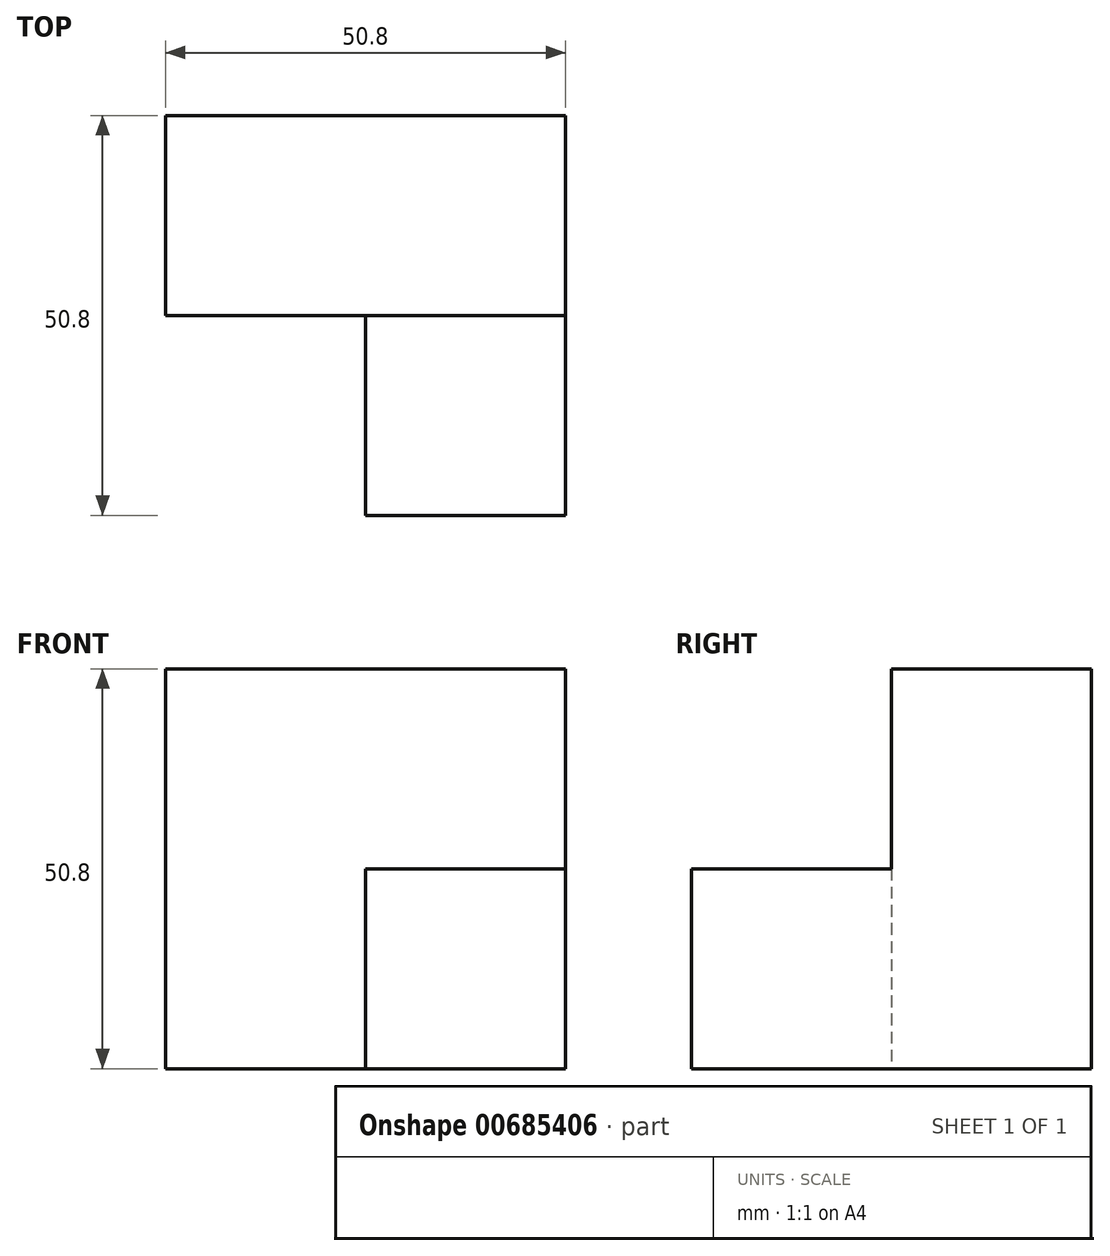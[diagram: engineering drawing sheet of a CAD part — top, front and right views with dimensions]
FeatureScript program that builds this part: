
annotation { "Feature Type Name" : "Feature", "Feature Type Description" : "" }
export const myFeature = defineFeature(function(context is Context, id is Id, definition is map)
    precondition{}
    {
        {
            var Q0;
            Q0=qCreatedBy(makeId("Front.planeOp"),FACE);
            var sketch = newSketch(context, id + "F0", { "sketchPlane" : qUnion([Q0])});
            skLineSegment(sketch, "E0", {"start": v(0, 0) * mm, "end": v(-50.8, 0) * mm});
            skLineSegment(sketch, "E1", {"start": v(-50.8, 0) * mm, "end": v(-50.8, 50.8) * mm});
            skLineSegment(sketch, "E2", {"start": v(-50.8, 50.8) * mm, "end": v(0, 50.8) * mm});
            skLineSegment(sketch, "E3", {"start": v(0, 50.8) * mm, "end": v(0, 0) * mm});
            skSolve(sketch);
        }
        {
            var Q0;
            Q0=makeQuery(id+"F0.imprint","IMPRINT",FACE,{"disambiguationData":[TD([[makeQuery(id+"F0.imprint","IMPRINT",EDGE,{"derivedFrom":sQuery(id+"F0.wireOp",EDGE,"E0")}),-1.0]])]});
            extrude(context, id + "F1", {"entities" : qUnion([Q0]), "depth" : 50.8 * mm, "offsetDistance" : 25.4 * mm});
        }
        {
            var Q0;
            Q0=makeQuery(id+"F1.opExtrude","CAP_FACE",FACE,{"disambiguationData":[OSD([sQuery(id+"F0.wireOp",EDGE,"E0"),sQuery(id+"F0.wireOp",EDGE,"E1"),sQuery(id+"F0.wireOp",EDGE,"E2"),sQuery(id+"F0.wireOp",EDGE,"E3")])],"isStart":false});
            var sketch = newSketch(context, id + "F2", { "sketchPlane" : qUnion([Q0])});
            skLineSegment(sketch, "E4.bottom", {"start": v(-50.8, 50.8) * mm, "end": v(-25.4, 50.8) * mm});
            skLineSegment(sketch, "E4.top", {"start": v(-50.8, 0) * mm, "end": v(-25.4, 0) * mm});
            skLineSegment(sketch, "E4.left", {"start": v(-50.8, 50.8) * mm, "end": v(-50.8, 0) * mm});
            skLineSegment(sketch, "E4.right", {"start": v(-25.4, 50.8) * mm, "end": v(-25.4, 0) * mm});
            skLineSegment(sketch, "E5.bottom", {"start": v(0, 50.8) * mm, "end": v(-25.4, 50.8) * mm});
            skLineSegment(sketch, "E5.top", {"start": v(0, 25.4) * mm, "end": v(-25.4, 25.4) * mm});
            skLineSegment(sketch, "E5.left", {"start": v(0, 50.8) * mm, "end": v(0, 25.4) * mm});
            skLineSegment(sketch, "E5.right", {"start": v(-25.4, 50.8) * mm, "end": v(-25.4, 25.4) * mm});
            skSolve(sketch);
        }
        {
            var Q0;
            Q0=makeQuery(id+"F2.imprint","IMPRINT",FACE,{"disambiguationData":[TD([[makeQuery(id+"F2.imprint","IMPRINT",EDGE,{"derivedFrom":sQuery(id+"F2.wireOp",EDGE,"E4.bottom")}),-1.0]])]});
            extrude(context, id + "F3", {"entities" : qUnion([Q0]), "operationType" : NewBodyOperationType.REMOVE, "oppositeDirection" : true, "depth" : 25.4 * mm, "offsetDistance" : 25.4 * mm});
        }
        {
            var Q0;
            Q0=makeQuery(id+"F1.opExtrude","CAP_FACE",FACE,{"disambiguationData":[OSD([sQuery(id+"F0.wireOp",EDGE,"E0"),sQuery(id+"F0.wireOp",EDGE,"E1"),sQuery(id+"F0.wireOp",EDGE,"E2"),sQuery(id+"F0.wireOp",EDGE,"E3")])],"isStart":false});
            var sketch = newSketch(context, id + "F4", { "sketchPlane" : qUnion([Q0])});
            skLineSegment(sketch, "E6.bottom", {"start": v(-25.4, 50.8) * mm, "end": v(0, 50.8) * mm});
            skLineSegment(sketch, "E6.top", {"start": v(-25.4, 25.4) * mm, "end": v(0, 25.4) * mm});
            skLineSegment(sketch, "E6.left", {"start": v(-25.4, 50.8) * mm, "end": v(-25.4, 25.4) * mm});
            skLineSegment(sketch, "E6.right", {"start": v(0, 50.8) * mm, "end": v(0, 25.4) * mm});
            skSolve(sketch);
        }
        {
            var Q0;
            Q0 = qSketchRegion(id + "F4", true);
            extrude(context, id + "F5", {"entities" : qUnion([Q0]), "operationType" : NewBodyOperationType.REMOVE, "oppositeDirection" : true, "depth" : 25.4 * mm, "offsetDistance" : 25.4 * mm});
        }
    });
